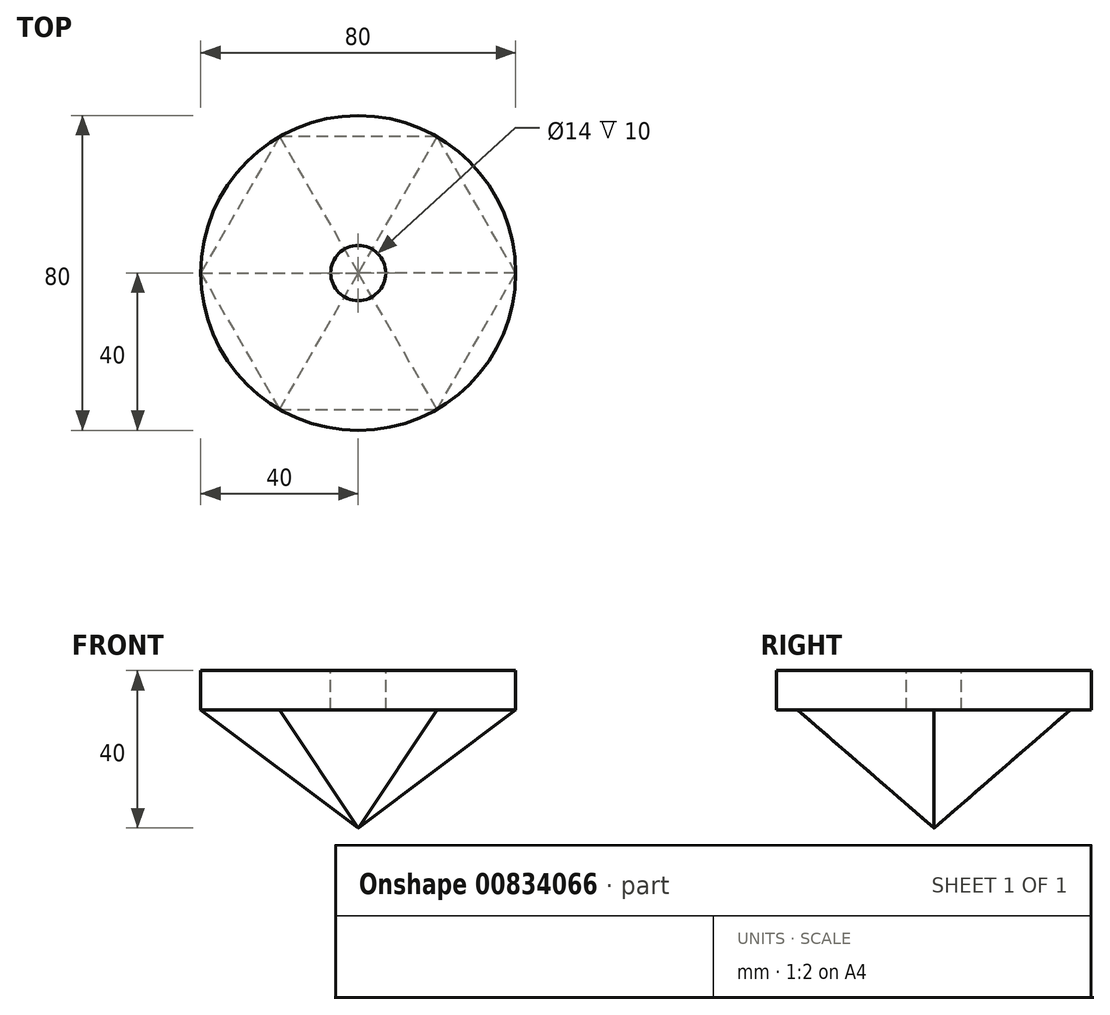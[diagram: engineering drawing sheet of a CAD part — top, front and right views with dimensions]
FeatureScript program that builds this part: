
annotation { "Feature Type Name" : "Feature", "Feature Type Description" : "" }
export const myFeature = defineFeature(function(context is Context, id is Id, definition is map)
    precondition{}
    {
        {
            var Q0;
            Q0=qCreatedBy(makeId("Top.planeOp"),FACE);
            var sketch = newSketch(context, id + "F0", { "sketchPlane" : qUnion([Q0])});
            skCircle(sketch, "E0", {"center": v(0, 0) * mm, "radius": 40 * mm});
            skSolve(sketch);
        }
        {
            var Q0;
            Q0 = qSketchRegion(id + "F0", true);
            extrude(context, id + "F1", {"entities" : qUnion([Q0]), "depth" : 40 * mm, "offsetDistance" : 25 * mm});
        }
        {
            var Q0;
            Q0=qCreatedBy(makeId("Top.planeOp"),FACE);
            var sketch = newSketch(context, id + "F2", { "sketchPlane" : qUnion([Q0])});
            skCircle(sketch, "E1.0", {"center": v(0, 0) * mm, "radius": 40 * mm});
            skSolve(sketch);
        }
        {
            var Q0;
            Q0 = qSketchRegion(id + "F2", true);
            extrude(context, id + "F3", {"entities" : qUnion([Q0]), "operationType" : NewBodyOperationType.REMOVE, "depth" : 30 * mm, "offsetDistance" : 25 * mm});
        }
        {
            var Q0;
            Q0=makeQuery(id+"F3.boolean.opBoolean","COPY",FACE,{"derivedFrom":makeQuery(id+"F3.opExtrude","CAP_FACE",FACE,{"disambiguationData":[OSD([sQuery(id+"F2.wireOp",EDGE,"E1.0")])],"isStart":false})});
            var sketch = newSketch(context, id + "F4", { "sketchPlane" : qUnion([Q0])});
            skCircle(sketch, "E2.cCircle", {"center": v(0, 0) * mm, "radius": 40 * mm, "construction": true});
            skLineSegment(sketch, "E2.0", {"start": v(40, 0) * mm, "end": v(20, -34.64) * mm});
            skLineSegment(sketch, "E2.1", {"start": v(20, -34.64) * mm, "end": v(-20, -34.64) * mm});
            skLineSegment(sketch, "E2.2", {"start": v(-20, -34.64) * mm, "end": v(-40, 0) * mm});
            skLineSegment(sketch, "E2.3", {"start": v(-40, 0) * mm, "end": v(-20, 34.64) * mm});
            skLineSegment(sketch, "E2.4", {"start": v(-20, 34.64) * mm, "end": v(20, 34.64) * mm});
            skLineSegment(sketch, "E2.5", {"start": v(20, 34.64) * mm, "end": v(40, 0) * mm});
            skSolve(sketch);
        }
        {
            var Q0;
            Q0=qCreatedBy(makeId("Top.planeOp"),FACE);
            var sketch = newSketch(context, id + "F5", { "sketchPlane" : qUnion([Q0])});
            skCircle(sketch, "E3", {"center": v(0, 0) * mm, "radius": 0.05 * mm});
            skSolve(sketch);
        }
        {
            var Q1;
            Q1 = qSketchRegion(id + "F4", true);
            var Q2;
            Q2 = qSketchRegion(id + "F5", true);
            loft(context, id + "F6", {"operationType" : NewBodyOperationType.ADD, "sheetProfilesArray" : [{ "sheetProfileEntities" : qUnion([Q1]) }, { "sheetProfileEntities" : qUnion([Q2]) }]});
        }
        {
            var Q0;
            Q0=makeQuery(id+"F1.opExtrude","CAP_FACE",FACE,{"disambiguationData":[OSD([sQuery(id+"F0.wireOp",EDGE,"E0")])],"isStart":false});
            var sketch = newSketch(context, id + "F7", { "sketchPlane" : qUnion([Q0])});
            skCircle(sketch, "E4", {"center": v(0, 0) * mm, "radius": 7 * mm});
            skSolve(sketch);
        }
        {
            var Q0;
            Q0 = qSketchRegion(id + "F7", true);
            extrude(context, id + "F8", {"entities" : qUnion([Q0]), "operationType" : NewBodyOperationType.REMOVE, "oppositeDirection" : true, "depth" : 10 * mm, "offsetDistance" : 25 * mm});
        }
    });
